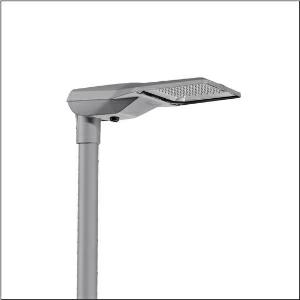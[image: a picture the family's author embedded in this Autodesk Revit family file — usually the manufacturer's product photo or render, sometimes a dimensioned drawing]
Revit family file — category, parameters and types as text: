
# Revit family: streetlight_sl_21_iq_midi___st1_0a_5xe3d31u08nb_218c
name_source: partatom
category: Lighting Fixtures
units: mm (PartAtom-declared; Revit-internal decimal feet)

## family parameters
Cut with Voids When Loaded = No
Host = Face
Light Source = No
Part Type = Normal
Room Calculation Point = No
Round Connector Dimension = Use Diameter
Shared = No

## types (1)
- --- (1 x LED, 21550 lm, 136.6 W, 3000K)
    Apparent Load = 137 VA
    CIE Flux Codes = 40 73 97 100 100
    Color Rendering = 70
    Color Temperature = 3000K
    Default Elevation = 1800 mm
    Description = Streetlight SL 21 iQ midi, mast luminaire, primary light control with lens, of PMMA, primary optical cover: cover, of toughened safety glass, transparent, light distribution: ST1.0a, light emission: direct distribution, primary light characteristic: asymmetric, installation type: post-top, side-entry, LED, High Power LED, rated luminous flux: 21.550lm, luminous efficacy: 158lm/W, light colour: 730, colour temperature: 3000K, control gear: iQ-Street Remote, D4i with power reduction, control: pre-setting: logarithmic dimming characteristic, Street-Remote, Auto-Match, Temp-Guard, Lumen-Switch, Night-Set, Smart-Wire, Light-Fading, Desk-Remote (wireless, voltage-free reading and setting of iQ features in the workshop via application-optimized NFC function/RFID function), optimised constant luminous flux control (CLO 2.0), mains connection: 230..240V, AC, 50/60Hz, start of lifetime: 137W, end of service life: 144W, reduction: 61W, luminaire housing, of diecast aluminium, powder-coated, SITECO metallic grey (DB 702S), corrosivity category C5 high according to DIN EN ISO 12944, please order mast flange separately, inclination adjustable: 0°, 5°, 10°, 15°, sealing non-destructively replaceable, multi-level sealing system, length: 644mm, width: 335mm, height: 110mm, mast flange for spigot size: 42mm (side-entry): 5XC10008XM4, 60/48mm (side-entry/post-top): 5XC10108XM2, 76/60mm (side-entry/post-top): 5XC10108XM1, mounting height: 4..8m, Smart Interface below, protection rating (complete): IP66, insulation class (complete): insulation class II (safety insulation), certification: CE, ENEC, ENEC+, VDE, impact resistance: IK10, permissible operating ambient temperature for outdoor applications: -40..+50°C, standard-compliant lighting for roads and squares, packaging unit: 1 piece

Light Distribution: ST1.0a
    Height = 111 mm
    Lamp = 1 x LED
    Lamp Light Flux = 21550 lm
    Lamp Power = 136.6 W
    Lamp count = 1
    Length = 644 mm
    Luminous efficacy = 158 lm/W
    Manufacturer = Siteco
    ModVariant = No
    Model = 5XE3D31U08NB
    Mounting Place = Pole
    Mounting Type = Pole top
    Number of Poles = 1
    OnlyDefault = Yes
    Power Factor = 1
    Product Name = Streetlight SL 21 iQ midi | ST1.0a
    Product group = mast luminaire | pylon top
    ProductGroupID = 6100
    Protection Class = Protection class II
    Protection Degree = IP 66
    RLX_Detail_Level = 1
    RLX_Emergency_Light_Flux = 0 lm
    RLX_Emergency_Type = 0
    RLX_Emergency_Type_DB = No
    RlxData = <blob elided: 91105 chars, md5=074e6c30>
    Socket = socket
    Standby Power = 0 W
    System Light Flux = 21550 lm
    System Power = 137 W
    Type Comments = factory setting: luminous flux: 100 % | dim-lin: 254 | 733 mA
    Type Image = l_1004300.jpg
    URL = http://relux.com
    VarID = @adj_115637
    Voltage = 0 V
    Weight = 0.00 kg
    Width = 336 mm

## geometry (parser evidence)
native form markers: Blend x4, Sweep x11
no freeform markers — native parametric forms only
